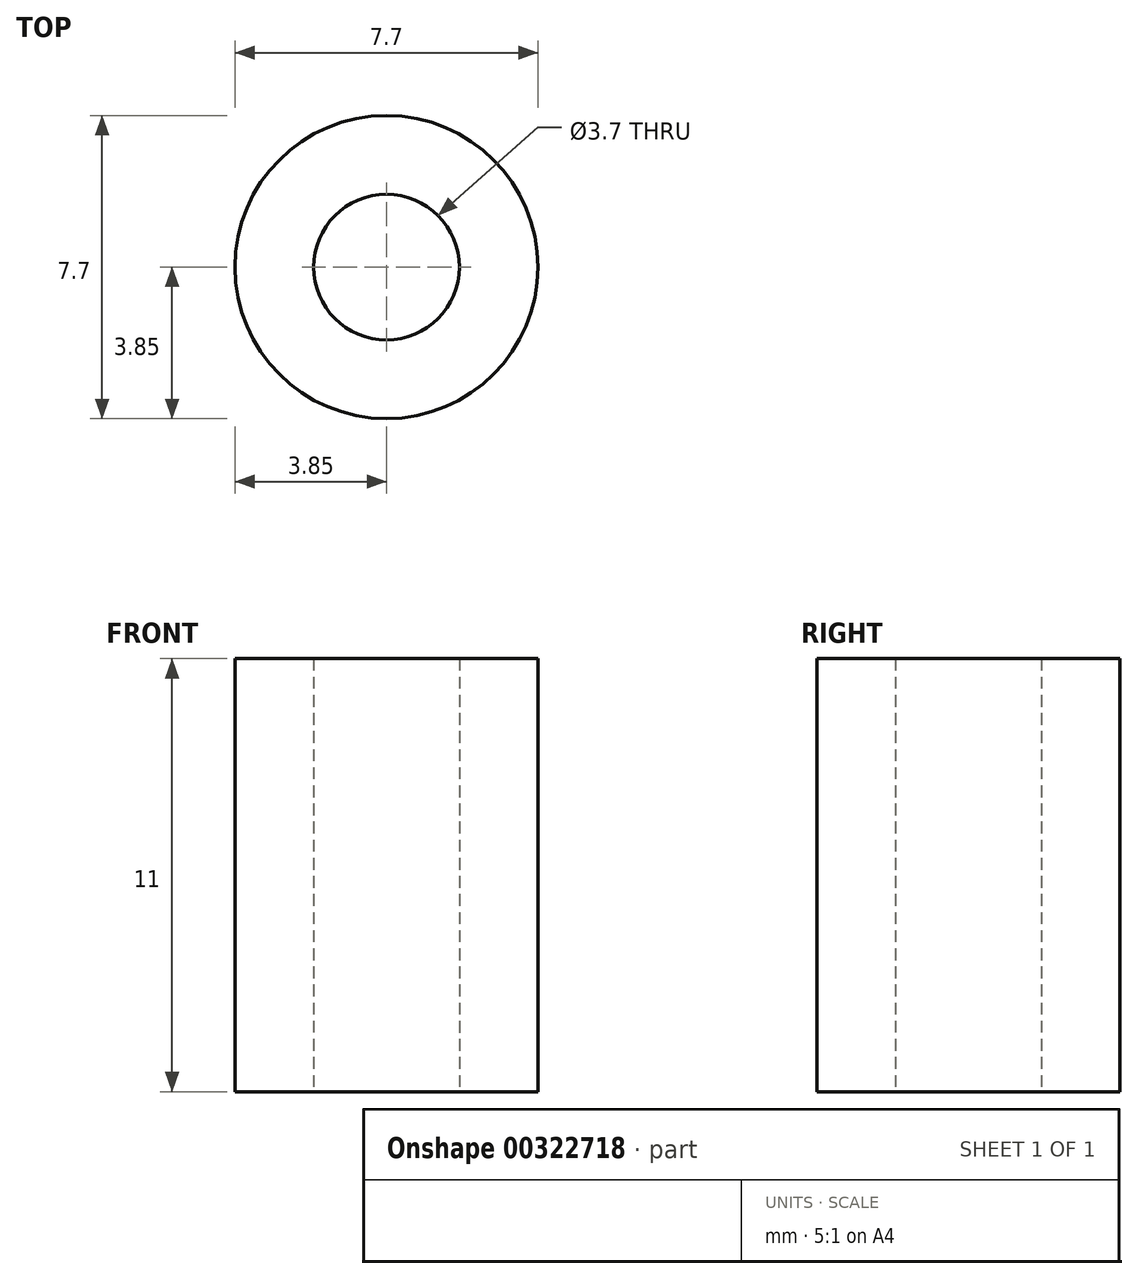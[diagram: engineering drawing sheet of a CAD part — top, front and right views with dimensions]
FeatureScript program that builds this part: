
annotation { "Feature Type Name" : "Feature", "Feature Type Description" : "" }
export const myFeature = defineFeature(function(context is Context, id is Id, definition is map)
    precondition{}
    {
        {
            var Q0;
            Q0=qCreatedBy(makeId("Top.planeOp"),FACE);
            var sketch = newSketch(context, id + "F0", { "sketchPlane" : qUnion([Q0])});
            skCircle(sketch, "E0", {"center": v(0, 0) * mm, "radius": 1.85 * mm});
            skCircle(sketch, "E1", {"center": v(0, 0) * mm, "radius": 3.85 * mm});
            skSolve(sketch);
        }
        {
            var Q0;
            Q0=makeQuery(id+"F0.imprint","IMPRINT",FACE,{"disambiguationData":[TD([[makeQuery(id+"F0.imprint","IMPRINT",EDGE,{"derivedFrom":sQuery(id+"F0.wireOp",EDGE,"E0")}),-1.0]])]});
            extrude(context, id + "F1", {"entities" : qUnion([Q0]), "depth" : 11 * mm, "offsetDistance" : 25 * mm});
        }
    });
